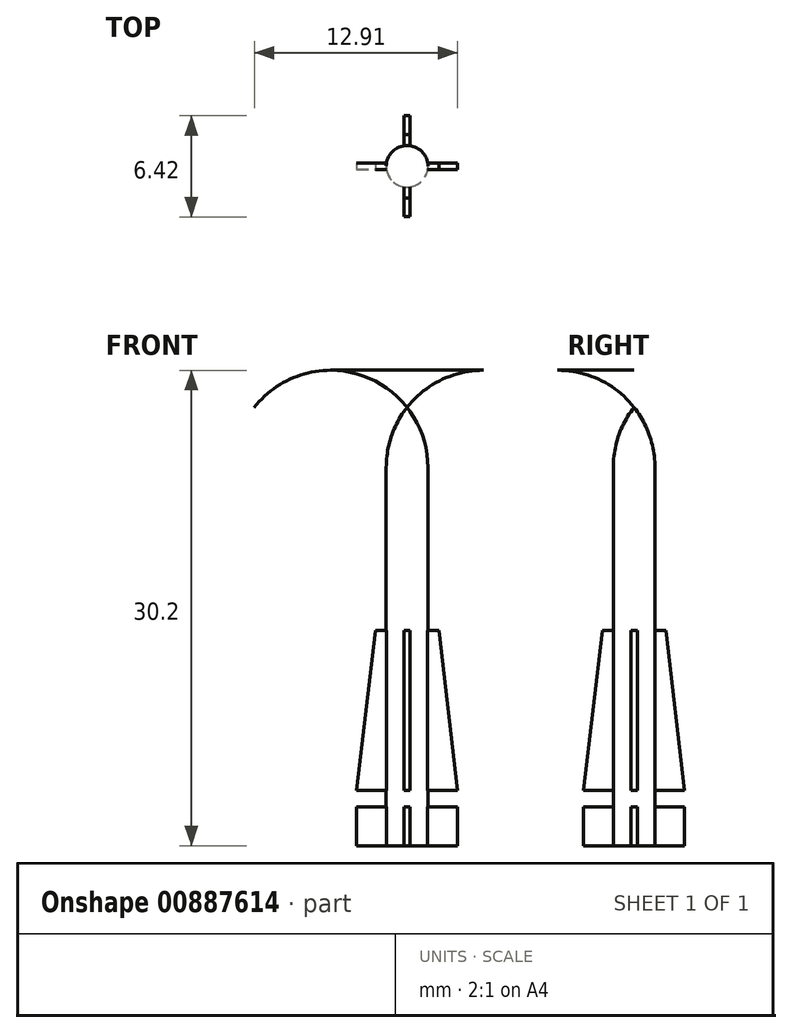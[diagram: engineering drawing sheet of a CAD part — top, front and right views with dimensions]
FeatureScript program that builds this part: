
annotation { "Feature Type Name" : "Feature", "Feature Type Description" : "" }
export const myFeature = defineFeature(function(context is Context, id is Id, definition is map)
    precondition{}
    {
        {
            var Q0;
            Q0=qCreatedBy(makeId("Front.planeOp"),FACE);
            var sketch = newSketch(context, id + "F0", { "sketchPlane" : qUnion([Q0])});
            skLineSegment(sketch, "E0", {"start": v(0, 0) * mm, "end": v(0, 27.85) * mm});
            skLineSegment(sketch, "E1", {"start": v(1.32, 24.03) * mm, "end": v(1.32, 0) * mm});
            skLineSegment(sketch, "E2", {"start": v(1.32, 0) * mm, "end": v(0, 0) * mm});
            skArc(sketch, "E3", {"start": v(1.32, 24.03) * mm, "mid": v(0.98, 26.05) * mm, "end": v(0, 27.85) * mm});
            skSolve(sketch);
        }
        {
            var Q0;
            {var subQ0=sQuery(id+"F0.wireOp",EDGE,"mrwio9nY-PsAZ-Zbfy-NhIU-sYq0QVbgGXAG");Q0=makeQuery(id+"F0.imprint","IMPRINT",FACE,{"disambiguationData":[TD([[makeQuery(id+"F0.imprint","IMPRINT",EDGE,{"derivedFrom":subQ0}),-1.0]])]});}
            var Q1;
            {var subQ7=sQuery(id+"F0.wireOp",EDGE,"E0");Q1=makeQuery(id+"F0.imprint","IMPRINT",FACE,{"disambiguationData":[TD([[makeQuery(id+"F0.imprint","IMPRINT",EDGE,{"derivedFrom":subQ7}),-1.0]])]});}
            var Q2;
            Q2=sQuery(id+"F0.wireOp",EDGE,"E0");
            revolve(context, id + "F1", {"surfaceOperationType" : NewSurfaceOperationType.NEW, "entities" : qUnion([Q0, Q1]), "axis" : qUnion([Q2]), "revolveType" : RevolveType.FULL});
        }
        {
            var Q0;
            Q0=qCreatedBy(makeId("Front.planeOp"),FACE);
            var sketch = newSketch(context, id + "F2", { "sketchPlane" : qUnion([Q0])});
            skLineSegment(sketch, "E4", {"start": v(0, 0) * mm, "end": v(0, 13.68) * mm});
            skLineSegment(sketch, "E5", {"start": v(0.4, 3.53) * mm, "end": v(0.4, 2.47) * mm});
            skLineSegment(sketch, "E6", {"start": v(0.4, 2.47) * mm, "end": v(3.2, 2.47) * mm});
            skLineSegment(sketch, "E7", {"start": v(1.32, 0) * mm, "end": v(1.32, 32.87) * mm, "construction": true});
            skLineSegment(sketch, "E8", {"start": v(0.4, 3.53) * mm, "end": v(3.2, 3.53) * mm});
            skLineSegment(sketch, "E9", {"start": v(3.2, 3.53) * mm, "end": v(2.01, 13.68) * mm});
            skLineSegment(sketch, "E10", {"start": v(0, 0) * mm, "end": v(3.2, 0) * mm});
            skLineSegment(sketch, "E11.0", {"start": v(-1.32, 24.03) * mm, "end": v(1.32, 24.03) * mm});
            skLineSegment(sketch, "E12", {"start": v(0, 13.68) * mm, "end": v(2.01, 13.68) * mm});
            skLineSegment(sketch, "E13", {"start": v(3.2, 2.47) * mm, "end": v(3.2, 0) * mm});
            skLineSegment(sketch, "E14.0", {"start": v(1.32, 0) * mm, "end": v(-1.32, 0) * mm});
            skSolve(sketch);
        }
        {
            var Q0;
            {var subQ0=sQuery(id+"F2.wireOp",EDGE,"E4");Q0=makeQuery(id+"F2.imprint","IMPRINT",FACE,{"disambiguationData":[TD([[makeQuery(id+"F2.imprint","IMPRINT",EDGE,{"derivedFrom":subQ0}),-1.0]])]});}
            extrude(context, id + "F3", {"entities" : qUnion([Q0]), "operationType" : NewBodyOperationType.ADD, "depth" : .4 * mm, "offsetDistance" : 25 * mm, "symmetric" : true});
        }
        {
            var Q0;
            Q0=makeQuery(id+"F1.opRevolve","SWEPT_BODY",BODY,{"disambiguationData":[OSD([sQuery(id+"F0.wireOp",EDGE,"E0"),sQuery(id+"F0.wireOp",EDGE,"E1"),sQuery(id+"F0.wireOp",EDGE,"E2"),sQuery(id+"F0.wireOp",EDGE,"2EiOItwe-9FNA-eY8p-DkXH-AMy5AHyUmzZA"),sQuery(id+"F0.wireOp",EDGE,"lF35QjYl-MEgV-fRWE-0Yr6-Bt5vS8A7brRf")])]});
            var Q1;
            Q1=makeQuery(id+"F1.opRevolve","SWEPT_FACE",FACE,{"disambiguationData":[OSD([sQuery(id+"F0.wireOp",EDGE,"E1")])]});
            circularPattern(context, id + "F4", {"operationType" : NewBodyOperationType.ADD, "entities" : qUnion([Q0]), "axis" : qUnion([Q1]), "angle" : 360 * degree, "instanceCount" : 4, "equalSpace" : true, "computeTransformsWithoutBuiltin" : true});
        }
    });
